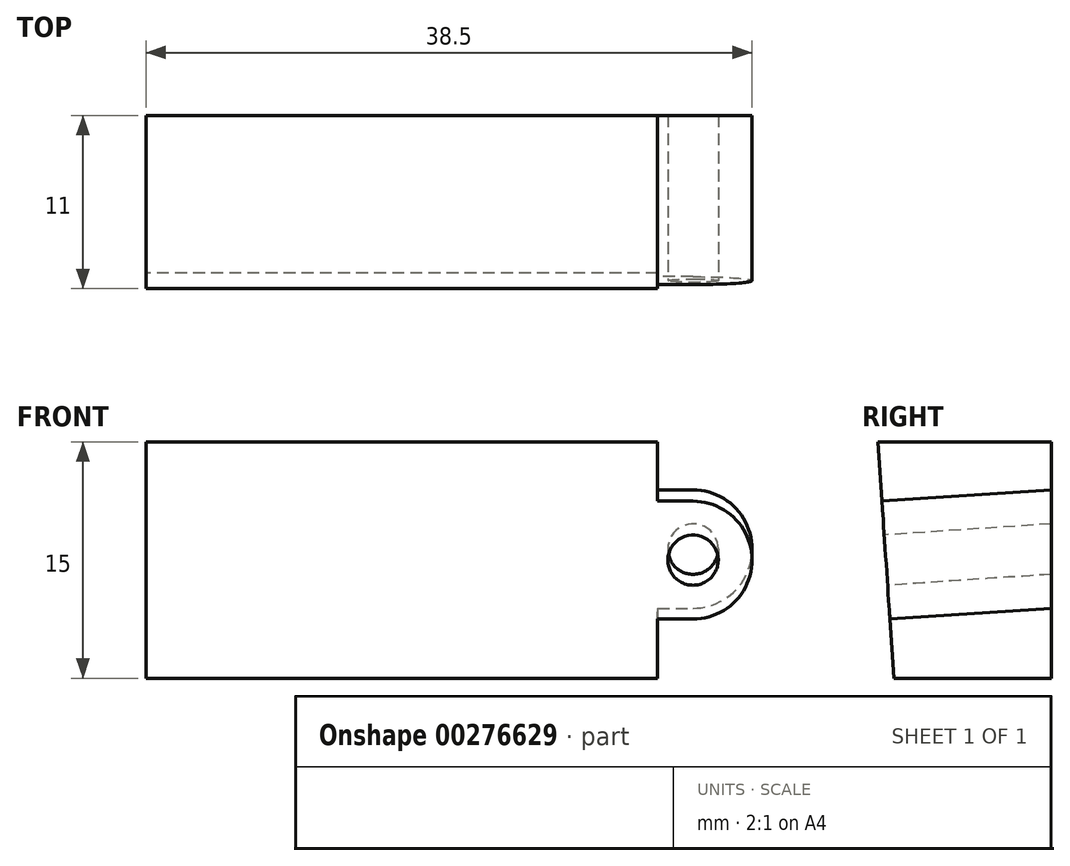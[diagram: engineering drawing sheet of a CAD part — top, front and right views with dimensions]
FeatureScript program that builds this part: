
annotation { "Feature Type Name" : "Feature", "Feature Type Description" : "" }
export const myFeature = defineFeature(function(context is Context, id is Id, definition is map)
    precondition{}
    {
        {
            var Q0;
            Q0=qCreatedBy(makeId("Right.planeOp"),FACE);
            var sketch = newSketch(context, id + "F0", { "sketchPlane" : qUnion([Q0])});
            skLineSegment(sketch, "E0", {"start": v(0, 0) * mm, "end": v(0, 15) * mm});
            skLineSegment(sketch, "E1", {"start": v(0, 15) * mm, "end": v(-11, 15) * mm});
            skLineSegment(sketch, "E2", {"start": v(-11, 15) * mm, "end": v(-10, 0) * mm});
            skLineSegment(sketch, "E3", {"start": v(-10, 0) * mm, "end": v(0, 0) * mm});
            skSolve(sketch);
        }
        {
            var Q0;
            Q0 = qSketchRegion(id + "F0", true);
            extrude(context, id + "F1", {"entities" : qUnion([Q0]), "endBound" : BoundingType.SYMMETRIC, "depth" : 32.5 * mm});
        }
        {
            var Q0;
            Q0=makeQuery(id+"F1.opExtrude","SWEPT_FACE",FACE,{"disambiguationData":[OSD([sQuery(id+"F0.wireOp",EDGE,"E2")])]});
            var sketch = newSketch(context, id + "F2", { "sketchPlane" : qUnion([Q0])});
            skLineSegment(sketch, "E4", {"start": v(0, 15.7) * mm, "end": v(0, 0.67) * mm, "construction": true});
            skLineSegment(sketch, "E5", {"start": v(0, 8.18) * mm, "end": v(18.5, 8.18) * mm, "construction": true});
            skCircle(sketch, "E6", {"center": v(18.5, 8.18) * mm, "radius": 1.6 * mm});
            skArc(sketch, "E7", {"start": v(18.5, 4.43) * mm, "mid": v(22.25, 8.18) * mm, "end": v(18.5, 11.93) * mm});
            skLineSegment(sketch, "E8", {"start": v(18.5, 8.18) * mm, "end": v(18.5, 11.93) * mm, "construction": true});
            skLineSegment(sketch, "E9", {"start": v(18.5, 11.93) * mm, "end": v(16.25, 11.93) * mm});
            skLineSegment(sketch, "E10", {"start": v(18.5, 8.18) * mm, "end": v(18.5, 4.43) * mm, "construction": true});
            skLineSegment(sketch, "E11", {"start": v(18.5, 4.43) * mm, "end": v(16.25, 4.43) * mm});
            skLineSegment(sketch, "E12.MirrorCS", {"start": v(-18.5, 8.18) * mm, "end": v(-18.5, 11.93) * mm, "construction": true});
            skLineSegment(sketch, "E13.MirrorCS", {"start": v(-18.5, 8.18) * mm, "end": v(-18.5, 4.43) * mm, "construction": true});
            skArc(sketch, "E14.MirrorCS", {"start": v(-18.5, 4.43) * mm, "mid": v(-22.25, 8.18) * mm, "end": v(-18.5, 11.93) * mm});
            skLineSegment(sketch, "E15.MirrorCS", {"start": v(-18.5, 11.93) * mm, "end": v(-16.25, 11.93) * mm});
            skCircle(sketch, "E16.MirrorC", {"center": v(-18.5, 8.18) * mm, "radius": 1.6 * mm});
            skLineSegment(sketch, "E17.MirrorCS", {"start": v(-18.5, 4.43) * mm, "end": v(-16.25, 4.43) * mm});
            skSolve(sketch);
        }
        {
            var Q0;
            Q0=makeQuery(id+"F2.imprint","IMPRINT",FACE,{"disambiguationData":[TD([[makeQuery(id+"F2.imprint","IMPRINT",EDGE,{"derivedFrom":sQuery(id+"F2.wireOp",EDGE,"E14.MirrorCS")}),-1.0]])]});
            var Q1;
            Q1=makeQuery(id+"F2.imprint","IMPRINT",FACE,{"disambiguationData":[TD([[makeQuery(id+"F2.imprint","IMPRINT",EDGE,{"derivedFrom":sQuery(id+"F2.wireOp",EDGE,"E6")}),-1.0]])]});
            var Q2;
            Q2=makeQuery(id+"F1.opExtrude","SWEPT_FACE",FACE,{"disambiguationData":[OSD([sQuery(id+"F0.wireOp",EDGE,"E0")])]});
            extrude(context, id + "F3", {"entities" : qUnion([Q0, Q1]), "operationType" : NewBodyOperationType.ADD, "endBound" : BoundingType.UP_TO_SURFACE, "oppositeDirection" : true, "endBoundEntityFace" : qUnion([Q2]), "depth" : 2.5 * mm});
        }
    });
